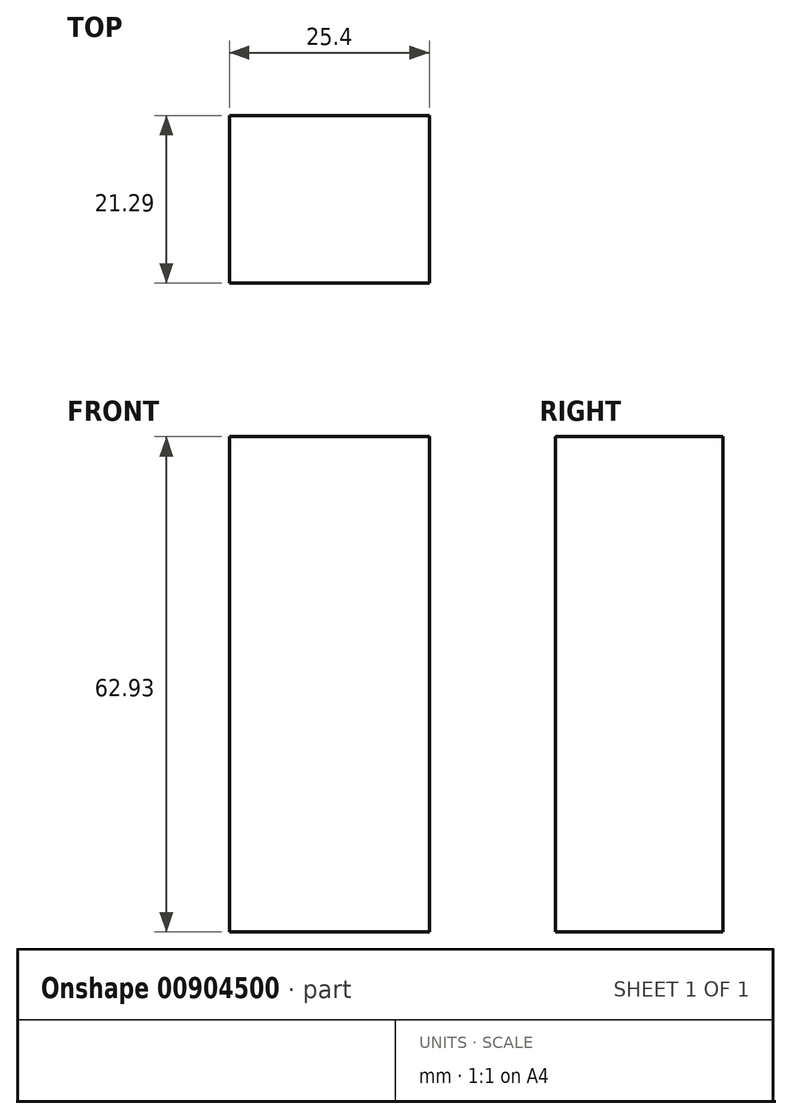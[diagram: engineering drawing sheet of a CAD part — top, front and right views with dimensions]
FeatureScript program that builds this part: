
annotation { "Feature Type Name" : "Feature", "Feature Type Description" : "" }
export const myFeature = defineFeature(function(context is Context, id is Id, definition is map)
    precondition{}
    {
        {
            var Q0;
            Q0=qCreatedBy(makeId("Right.planeOp"),FACE);
            var sketch = newSketch(context, id + "F0", { "sketchPlane" : qUnion([Q0])});
            skLineSegment(sketch, "E0.bottom", {"start": v(-41.6, 30.18) * mm, "end": v(-20.32, 30.18) * mm});
            skLineSegment(sketch, "E0.top", {"start": v(-41.6, 93.11) * mm, "end": v(-20.32, 93.11) * mm});
            skLineSegment(sketch, "E0.left", {"start": v(-41.6, 30.18) * mm, "end": v(-41.6, 93.11) * mm});
            skLineSegment(sketch, "E0.right", {"start": v(-20.32, 30.18) * mm, "end": v(-20.32, 93.11) * mm});
            skLineSegment(sketch, "E1.bottom", {"start": v(-7.59, 9.82) * mm, "end": v(-20.32, 9.82) * mm});
            skLineSegment(sketch, "E1.top", {"start": v(-7.59, 0) * mm, "end": v(-20.32, 0) * mm});
            skLineSegment(sketch, "E1.left", {"start": v(-7.59, 9.82) * mm, "end": v(-7.59, 0) * mm});
            skLineSegment(sketch, "E1.right", {"start": v(-20.32, 9.82) * mm, "end": v(-20.32, 0) * mm});
            skLineSegment(sketch, "E2.bottom", {"start": v(-30.32, -24.8) * mm, "end": v(-15.12, -24.8) * mm});
            skLineSegment(sketch, "E2.top", {"start": v(-30.32, -50.94) * mm, "end": v(-15.12, -50.94) * mm});
            skLineSegment(sketch, "E2.left", {"start": v(-30.32, -24.8) * mm, "end": v(-30.32, -50.94) * mm});
            skLineSegment(sketch, "E2.right", {"start": v(-15.12, -24.8) * mm, "end": v(-15.12, -50.94) * mm});
            skSolve(sketch);
        }
        {
            var Q0;
            Q0=makeQuery(id+"F0.imprint","IMPRINT",FACE,{"disambiguationData":[TD([[makeQuery(id+"F0.imprint","IMPRINT",EDGE,{"derivedFrom":sQuery(id+"F0.wireOp",EDGE,"E0.bottom")}),1.0]])]});
            extrude(context, id + "F1", {"entities" : qUnion([Q0]), "depth" : 25.4 * mm, "offsetDistance" : 25.4 * mm});
        }
    });
